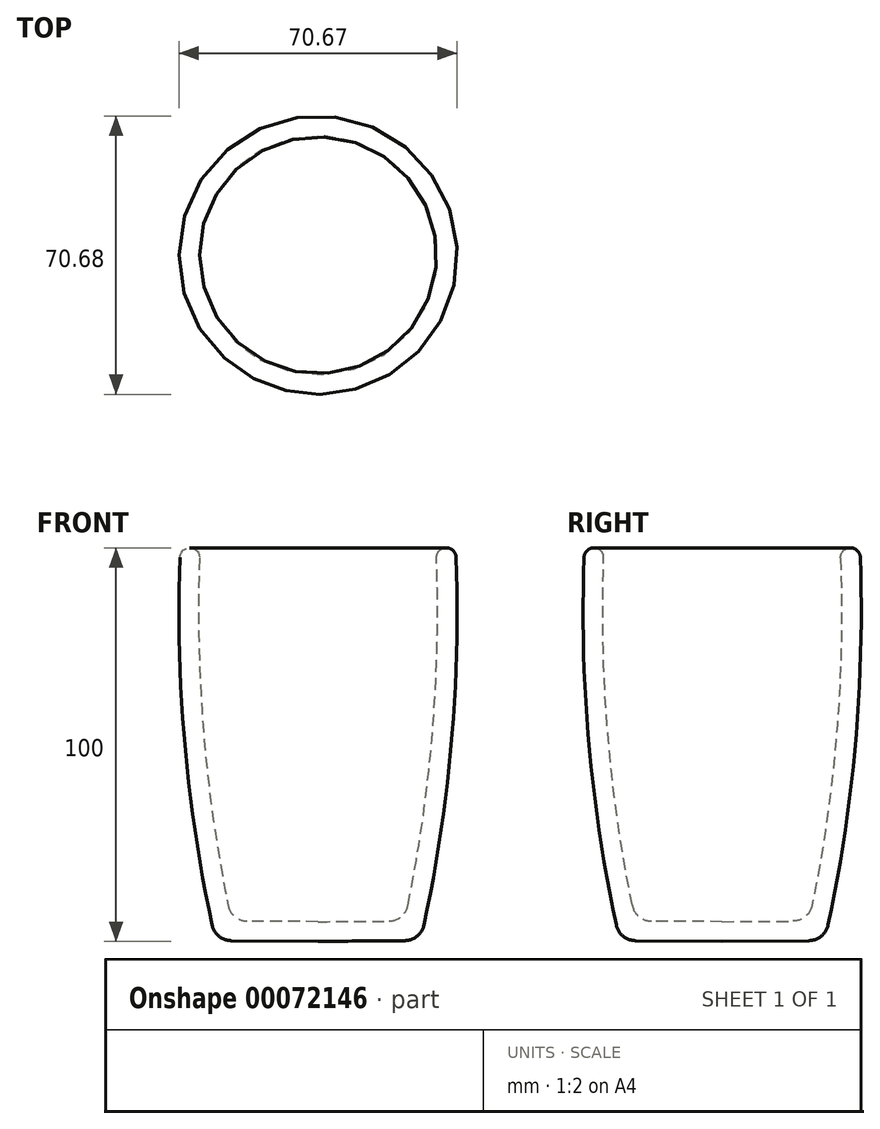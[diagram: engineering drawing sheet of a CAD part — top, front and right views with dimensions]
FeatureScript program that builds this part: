
annotation { "Feature Type Name" : "Feature", "Feature Type Description" : "" }
export const myFeature = defineFeature(function(context is Context, id is Id, definition is map)
    precondition{}
    {
        {
            var Q0;
            Q0=qCreatedBy(makeId("Front.planeOp"),FACE);
            var sketch = newSketch(context, id + "F0", { "sketchPlane" : qUnion([Q0])});
            skLineSegment(sketch, "E0", {"start": v(-91.18, 0) * mm, "end": v(-91.18, -100) * mm});
            skLineSegment(sketch, "E1", {"start": v(-91.18, 0) * mm, "end": v(-126.18, 0) * mm});
            skArc(sketch, "E2", {"start": v(-126.18, 0) * mm, "mid": v(-124.99, -50.18) * mm, "end": v(-117.23, -99.78) * mm});
            skLineSegment(sketch, "E3", {"start": v(-117.23, -99.78) * mm, "end": v(-91.18, -100) * mm});
            skSolve(sketch);
        }
        {
            var Q0;
            Q0=makeQuery(id+"F0.imprint","IMPRINT",FACE,{"disambiguationData":[TD([[makeQuery(id+"F0.imprint","IMPRINT",EDGE,{"derivedFrom":sQuery(id+"F0.wireOp",EDGE,"E0")}),-1.0]])]});
            var Q1;
            Q1=sQuery(id+"F0.wireOp",EDGE,"E0");
            revolve(context, id + "F1", {"entities" : qUnion([Q0]), "axis" : qUnion([Q1]), "revolveType" : RevolveType.FULL});
        }
        {
            var Q0;
            Q0=makeQuery(id+"F1.opRevolve","SWEPT_FACE",FACE,{"disambiguationData":[OSD([sQuery(id+"F0.wireOp",EDGE,"E1")])]});
            shell(context, id + "F2", {"entities" : qUnion([Q0]), "thickness" : 5 * mm});
        }
        {
            var Q0;
            Q0=makeQuery(id+"F1.opRevolve","SWEPT_EDGE",EDGE,{"disambiguationData":[OSD([sQuery(id+"F0.wireOp",EDGE,"E1"),sQuery(id+"F0.wireOp",EDGE,"E2")])]});
            var Q1;
            Q1=makeQuery(id+"F2.opShell","OFFSET_EDGE",EDGE,{"disambiguationData":[OSD([sQuery(id+"F0.wireOp",EDGE,"E1"),sQuery(id+"F0.wireOp",EDGE,"E2")])]});
            fillet(context, id + "F3", {"entities" : qUnion([Q0, Q1]), "radius" : 2.5 * mm, "tangentPropagation" : true, "allowEdgeOverflow" : false});
        }
        {
            var Q0;
            Q0=makeQuery(id+"F1.opRevolve","SWEPT_EDGE",EDGE,{"disambiguationData":[OSD([sQuery(id+"F0.wireOp",EDGE,"E2"),sQuery(id+"F0.wireOp",EDGE,"E3")])]});
            fillet(context, id + "F4", {"entities" : qUnion([Q0]), "radius" : 5 * mm, "tangentPropagation" : true, "allowEdgeOverflow" : false});
        }
        {
            var Q0;
            Q0=makeQuery(id+"F2.opShell","OFFSET_EDGE",EDGE,{"disambiguationData":[OSD([sQuery(id+"F0.wireOp",EDGE,"E2"),sQuery(id+"F0.wireOp",EDGE,"E3")])]});
            fillet(context, id + "F5", {"entities" : qUnion([Q0]), "radius" : 5 * mm, "tangentPropagation" : true, "allowEdgeOverflow" : false});
        }
    });
